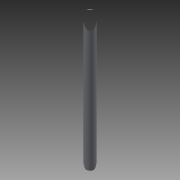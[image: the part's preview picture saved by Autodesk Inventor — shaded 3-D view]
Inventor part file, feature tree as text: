
AUTODESK INVENTOR PART (.ipt)
format: ipt  version: 2015 (Build 190159000, 159)  size: 62,976 bytes
history: native  units: in
note: dims shown in document units (in); Inventor stores cm internally (conversion verified against a paired STEP export)
features: extrude x1, sketch x1
ambient origin geometry x8: Origin, YZ Plane, XZ Plane, XY Plane, X Axis, Y Axis, Z Axis, Center Point
bodies: Solid1 (feature_tree)
feature tree (2):
  extrude  "Extrusion1"  Depth=5.1875in TaperAngle=0.0deg
  sketch  "Sketch1"  dims[d0=0.25in d1=5.1875in d2=0.0in]
